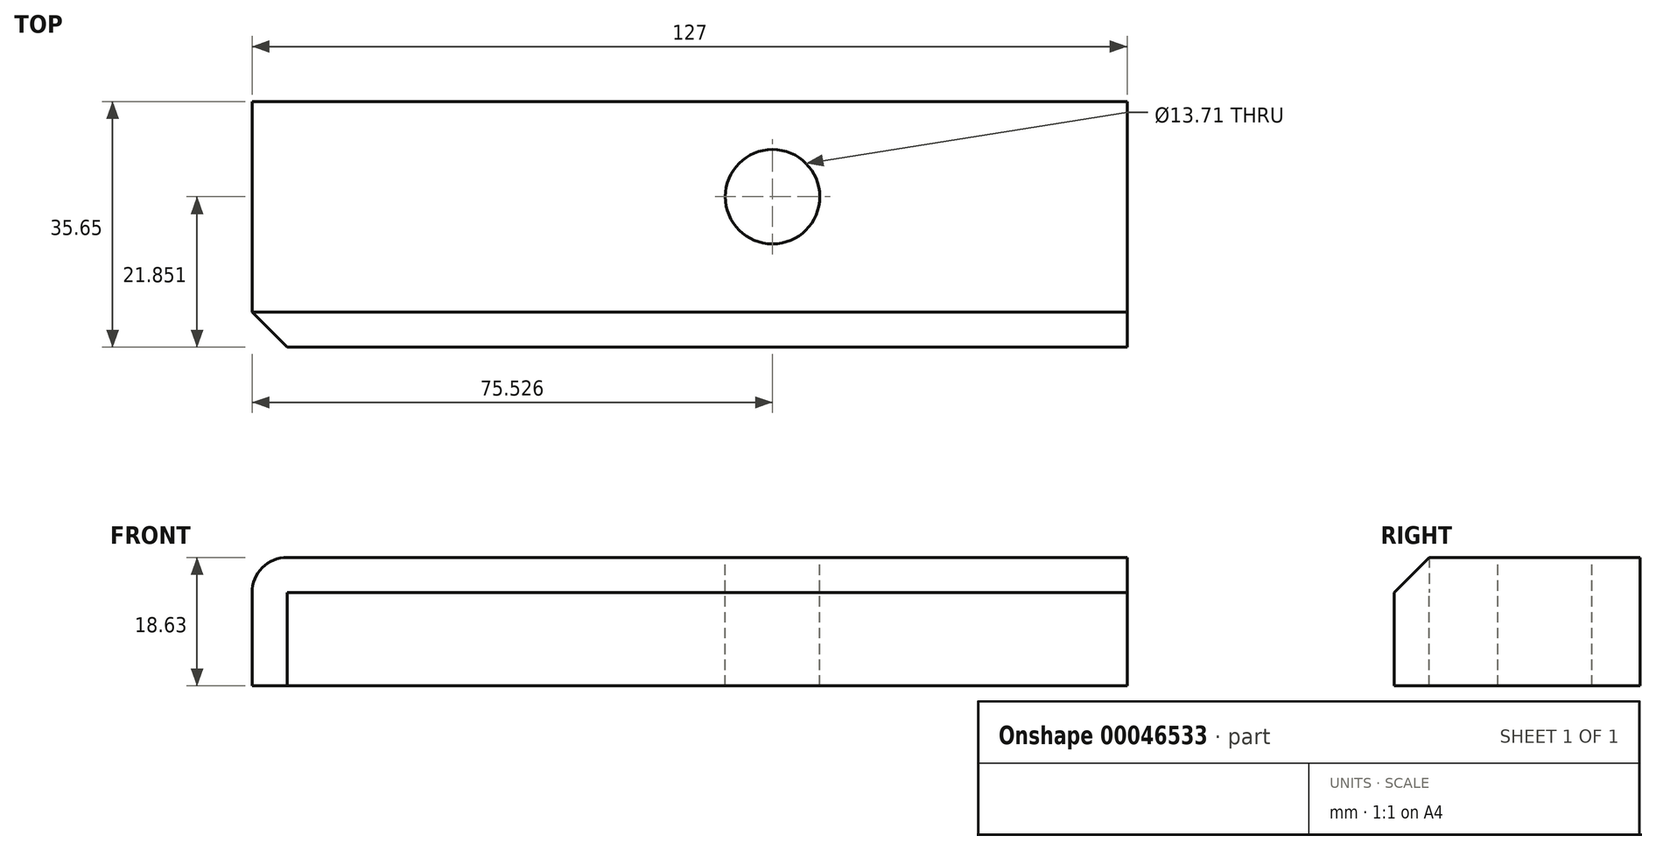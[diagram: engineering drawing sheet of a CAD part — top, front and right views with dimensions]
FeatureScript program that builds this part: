
annotation { "Feature Type Name" : "Feature", "Feature Type Description" : "" }
export const myFeature = defineFeature(function(context is Context, id is Id, definition is map)
    precondition{}
    {
        {
            var Q0;
            Q0=qCreatedBy(makeId("Right.planeOp"),FACE);
            var sketch = newSketch(context, id + "F0", { "sketchPlane" : qUnion([Q0])});
            skLineSegment(sketch, "E0.bottom", {"start": v(-59.08, -43.76) * mm, "end": v(-23.43, -43.76) * mm});
            skLineSegment(sketch, "E0.top", {"start": v(-59.08, -25.13) * mm, "end": v(-23.43, -25.13) * mm});
            skLineSegment(sketch, "E0.left", {"start": v(-59.08, -43.76) * mm, "end": v(-59.08, -25.13) * mm});
            skLineSegment(sketch, "E0.right", {"start": v(-23.43, -43.76) * mm, "end": v(-23.43, -25.13) * mm});
            skSolve(sketch);
        }
        {
            var Q0;
            Q0 = qSketchRegion(id + "F0", true);
            extrude(context, id + "F1", {"entities" : qUnion([Q0]), "depth" : 127 * mm});
        }
        {
            var Q0;
            Q0=makeQuery(id+"F1.opExtrude","SWEPT_FACE",FACE,{"disambiguationData":[OSD([sQuery(id+"F0.wireOp",EDGE,"E0.top")])]});
            var sketch = newSketch(context, id + "F2", { "sketchPlane" : qUnion([Q0])});
            skCircle(sketch, "E1", {"center": v(75.53, -37.23) * mm, "radius": 6.85 * mm});
            skPoint(sketch, "E1.first.point", {"position": v(68.8, -35.95) * mm});
            skPoint(sketch, "E1.second.point", {"position": v(76.8, -43.96) * mm});
            skPoint(sketch, "E1.third.point", {"position": v(82.14, -35.42) * mm});
            skSolve(sketch);
        }
        {
            var Q0;
            Q0=makeQuery(id+"F2.imprint","IMPRINT",FACE,{"disambiguationData":[TD([[makeQuery(id+"F2.imprint","IMPRINT",EDGE,{"derivedFrom":sQuery(id+"F2.wireOp",EDGE,"E1")}),1.0]])]});
            extrude(context, id + "F3", {"entities" : qUnion([Q0]), "operationType" : NewBodyOperationType.REMOVE, "oppositeDirection" : true, "depth" : 25.4 * mm});
        }
        {
            var Q0;
            Q0=makeQuery(id+"F1.opExtrude","CAP_EDGE",EDGE,{"disambiguationData":[OSD([sQuery(id+"F0.wireOp",EDGE,"E0.top")])],"isStart":true});
            fillet(context, id + "F4", {"entities" : qUnion([Q0]), "radius" : 5.08 * mm, "tangentPropagation" : true, "allowEdgeOverflow" : false});
        }
        {
            var Q0;
            Q0=makeQuery(id+"F1.opExtrude","SWEPT_EDGE",EDGE,{"disambiguationData":[OSD([sQuery(id+"F0.wireOp",EDGE,"E0.top"),sQuery(id+"F0.wireOp",EDGE,"E0.left")])]});
            chamfer(context, id + "F5", {"entities" : qUnion([Q0]), "width" : 5.08 * mm, "tangentPropagation" : true});
        }
    });
